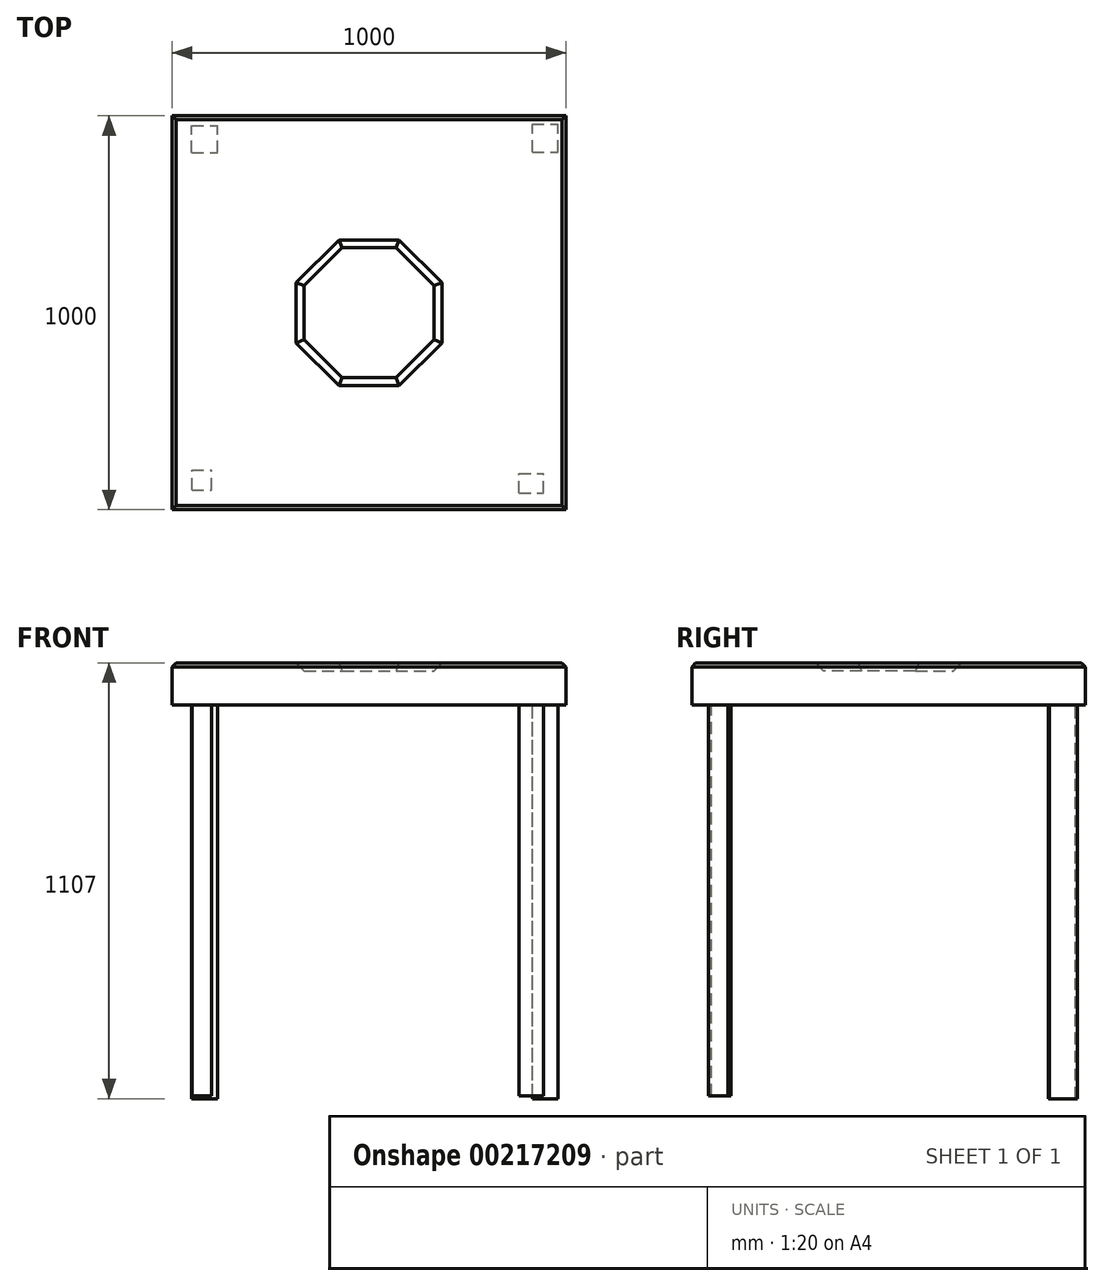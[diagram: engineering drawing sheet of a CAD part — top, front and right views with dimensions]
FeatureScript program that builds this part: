
annotation { "Feature Type Name" : "Feature", "Feature Type Description" : "" }
export const myFeature = defineFeature(function(context is Context, id is Id, definition is map)
    precondition{}
    {
        {
            var Q0;
            Q0=qCreatedBy(makeId("Top.planeOp"),FACE);
            var sketch = newSketch(context, id + "F0", { "sketchPlane" : qUnion([Q0])});
            skLineSegment(sketch, "E0.bottom", {"start": v(500, -500) * mm, "end": v(-500, -500) * mm});
            skLineSegment(sketch, "E0.top", {"start": v(500, 500) * mm, "end": v(-500, 500) * mm});
            skLineSegment(sketch, "E0.left", {"start": v(500, -500) * mm, "end": v(500, 500) * mm});
            skLineSegment(sketch, "E0.right", {"start": v(-500, -500) * mm, "end": v(-500, 500) * mm});
            skPoint(sketch, "E0.middle", {"position": v(0, 0) * mm});
            skSolve(sketch);
        }
        {
            var Q0;
            Q0=makeQuery(id+"F0.imprint","IMPRINT",FACE,{"disambiguationData":[TD([[makeQuery(id+"F0.imprint","IMPRINT",EDGE,{"derivedFrom":sQuery(id+"F0.wireOp",EDGE,"E0.bottom")}),-1.0]])]});
            extrude(context, id + "F1", {"entities" : qUnion([Q0]), "depth" : 100 * mm});
        }
        {
            var Q0;
            Q0=makeQuery(id+"F1.opExtrude","CAP_FACE",FACE,{"disambiguationData":[OSD([sQuery(id+"F0.wireOp",EDGE,"E0.bottom"),sQuery(id+"F0.wireOp",EDGE,"E0.top"),sQuery(id+"F0.wireOp",EDGE,"E0.left"),sQuery(id+"F0.wireOp",EDGE,"E0.right")])],"isStart":false});
            var sketch = newSketch(context, id + "F2", { "sketchPlane" : qUnion([Q0])});
            skCircle(sketch, "E1.cCircle", {"center": v(0, 0) * mm, "radius": 175 * mm, "construction": true});
            skLineSegment(sketch, "E1.0", {"start": v(175, -72.49) * mm, "end": v(72.49, -175) * mm});
            skLineSegment(sketch, "E1.1", {"start": v(72.49, -175) * mm, "end": v(-72.49, -175) * mm});
            skLineSegment(sketch, "E1.2", {"start": v(-72.49, -175) * mm, "end": v(-175, -72.49) * mm});
            skLineSegment(sketch, "E1.3", {"start": v(-175, -72.49) * mm, "end": v(-175, 72.49) * mm});
            skLineSegment(sketch, "E1.4", {"start": v(-175, 72.49) * mm, "end": v(-72.49, 175) * mm});
            skLineSegment(sketch, "E1.5", {"start": v(-72.49, 175) * mm, "end": v(72.49, 175) * mm});
            skLineSegment(sketch, "E1.6", {"start": v(72.49, 175) * mm, "end": v(175, 72.49) * mm});
            skLineSegment(sketch, "E1.7", {"start": v(175, 72.49) * mm, "end": v(175, -72.49) * mm});
            skPoint(sketch, "E1.0.midPoint", {"position": v(123.74, -123.74) * mm});
            skSolve(sketch);
        }
        {
            var Q0;
            Q0=makeQuery(id+"F2.imprint","IMPRINT",FACE,{"disambiguationData":[TD([[makeQuery(id+"F2.imprint","IMPRINT",EDGE,{"derivedFrom":sQuery(id+"F2.wireOp",EDGE,"E1.0")}),-1.0]])]});
            extrude(context, id + "F3", {"entities" : qUnion([Q0]), "operationType" : NewBodyOperationType.REMOVE, "oppositeDirection" : true, "depth" : 20 * mm});
        }
        {
            var Q0;
            Q0=makeQuery(id+"F3.boolean.opBoolean","COPY",FACE,{"derivedFrom":makeQuery(id+"F3.opExtrude","CAP_FACE",FACE,{"disambiguationData":[OSD([sQuery(id+"F2.wireOp",EDGE,"E1.0"),sQuery(id+"F2.wireOp",EDGE,"E1.1"),sQuery(id+"F2.wireOp",EDGE,"E1.2"),sQuery(id+"F2.wireOp",EDGE,"E1.3"),sQuery(id+"F2.wireOp",EDGE,"E1.4"),sQuery(id+"F2.wireOp",EDGE,"E1.5"),sQuery(id+"F2.wireOp",EDGE,"E1.6"),sQuery(id+"F2.wireOp",EDGE,"E1.7")])],"isStart":false})});
            var Q1;
            Q1=makeQuery(id+"F1.opExtrude","CAP_FACE",FACE,{"disambiguationData":[OSD([sQuery(id+"F0.wireOp",EDGE,"E0.bottom"),sQuery(id+"F0.wireOp",EDGE,"E0.top"),sQuery(id+"F0.wireOp",EDGE,"E0.left"),sQuery(id+"F0.wireOp",EDGE,"E0.right")])],"isStart":false});
            chamfer(context, id + "F4", {"entities" : qUnion([Q0, Q1]), "width" : 10 * mm, "tangentPropagation" : true});
        }
        {
            var Q0;
            Q0=makeQuery(id+"F1.opExtrude","CAP_FACE",FACE,{"disambiguationData":[OSD([sQuery(id+"F0.wireOp",EDGE,"E0.bottom"),sQuery(id+"F0.wireOp",EDGE,"E0.top"),sQuery(id+"F0.wireOp",EDGE,"E0.left"),sQuery(id+"F0.wireOp",EDGE,"E0.right")])],"isStart":true});
            var sketch = newSketch(context, id + "F5", { "sketchPlane" : qUnion([Q0])});
            skLineSegment(sketch, "E2.bottom", {"start": v(-450, 450) * mm, "end": v(-400, 450) * mm});
            skLineSegment(sketch, "E2.top", {"start": v(-450, 400) * mm, "end": v(-400, 400) * mm});
            skLineSegment(sketch, "E2.left", {"start": v(-450, 450) * mm, "end": v(-450, 400) * mm});
            skLineSegment(sketch, "E2.right", {"start": v(-400, 450) * mm, "end": v(-400, 400) * mm});
            skSolve(sketch);
        }
        {
            var Q0;
            Q0 = qSketchRegion(id + "F5", true);
            extrude(context, id + "F6", {"entities" : qUnion([Q0]), "operationType" : NewBodyOperationType.ADD, "depth" : 1000 * mm});
        }
        {
            var Q0;
            Q0=makeQuery(id+"F1.opExtrude","CAP_FACE",FACE,{"disambiguationData":[OSD([sQuery(id+"F0.wireOp",EDGE,"E0.bottom"),sQuery(id+"F0.wireOp",EDGE,"E0.top"),sQuery(id+"F0.wireOp",EDGE,"E0.left"),sQuery(id+"F0.wireOp",EDGE,"E0.right")])],"isStart":true});
            var sketch = newSketch(context, id + "F7", { "sketchPlane" : qUnion([Q0])});
            skLineSegment(sketch, "E3.bottom", {"start": v(381.33, 458.2) * mm, "end": v(443, 458.2) * mm});
            skLineSegment(sketch, "E3.top", {"start": v(381.33, 408.2) * mm, "end": v(443, 408.2) * mm});
            skLineSegment(sketch, "E3.left", {"start": v(381.33, 458.2) * mm, "end": v(381.33, 408.2) * mm});
            skLineSegment(sketch, "E3.right", {"start": v(443, 458.2) * mm, "end": v(443, 408.2) * mm});
            skLineSegment(sketch, "E4.bottom", {"start": v(381.33, 408.2) * mm, "end": v(381.33, 408.2) * mm});
            skLineSegment(sketch, "E4.top", {"start": v(381.33, 458.2) * mm, "end": v(381.33, 458.2) * mm});
            skLineSegment(sketch, "E4.left", {"start": v(381.33, 408.2) * mm, "end": v(381.33, 458.2) * mm});
            skLineSegment(sketch, "E4.right", {"start": v(381.33, 408.2) * mm, "end": v(381.33, 458.2) * mm});
            skLineSegment(sketch, "E5.bottom", {"start": v(-457.1, -413.8) * mm, "end": v(-407.1, -413.8) * mm});
            skLineSegment(sketch, "E5.top", {"start": v(-457.1, -463.8) * mm, "end": v(-407.1, -463.8) * mm});
            skLineSegment(sketch, "E5.left", {"start": v(-457.1, -413.8) * mm, "end": v(-457.1, -463.8) * mm});
            skLineSegment(sketch, "E5.right", {"start": v(-407.1, -413.8) * mm, "end": v(-407.1, -463.8) * mm});
            skLineSegment(sketch, "E6.bottom", {"start": v(388.25, -419.8) * mm, "end": v(455.2, -419.8) * mm});
            skLineSegment(sketch, "E6.top", {"start": v(388.25, -463.8) * mm, "end": v(455.2, -463.8) * mm});
            skLineSegment(sketch, "E6.left", {"start": v(388.25, -419.8) * mm, "end": v(388.25, -463.8) * mm});
            skLineSegment(sketch, "E6.right", {"start": v(455.2, -419.8) * mm, "end": v(455.2, -463.8) * mm});
            skLineSegment(sketch, "E7.bottom", {"start": v(388.25, -463.8) * mm, "end": v(388.25, -463.8) * mm});
            skLineSegment(sketch, "E7.top", {"start": v(388.25, -419.8) * mm, "end": v(388.25, -419.8) * mm});
            skLineSegment(sketch, "E7.left", {"start": v(388.25, -463.8) * mm, "end": v(388.25, -419.8) * mm});
            skLineSegment(sketch, "E7.right", {"start": v(388.25, -463.8) * mm, "end": v(388.25, -419.8) * mm});
            skSolve(sketch);
        }
        {
            var Q0;
            Q0=makeQuery(id+"F7.imprint","IMPRINT",FACE,{"disambiguationData":[TD([[makeQuery(id+"F7.imprint","IMPRINT",EDGE,{"derivedFrom":sQuery(id+"F7.wireOp",EDGE,"E3.bottom")}),-1.0]])]});
            extrude(context, id + "F8", {"entities" : qUnion([Q0]), "operationType" : NewBodyOperationType.ADD, "depth" : 1000 * mm});
        }
        {
            var Q0;
            Q0=makeQuery(id+"F1.opExtrude","CAP_FACE",FACE,{"disambiguationData":[OSD([sQuery(id+"F0.wireOp",EDGE,"E0.bottom"),sQuery(id+"F0.wireOp",EDGE,"E0.top"),sQuery(id+"F0.wireOp",EDGE,"E0.left"),sQuery(id+"F0.wireOp",EDGE,"E0.right")])],"isStart":true});
            var sketch = newSketch(context, id + "F9", { "sketchPlane" : qUnion([Q0])});
            skSolve(sketch);
        }
        {
            var Q0;
            Q0=makeQuery(id+"F9.imprint","IMPRINT",FACE,{"disambiguationData":[TD([[makeQuery(id+"F9.imprint","IMPRINT",EDGE,{"derivedFrom":makeQuery(id+"F1.opExtrude","CAP_EDGE",EDGE,{"disambiguationData":[OSD([sQuery(id+"F0.wireOp",EDGE,"E0.bottom")])],"isStart":true})}),1.0]])]});
            var sketch = newSketch(context, id + "F10", { "sketchPlane" : qUnion([Q0])});
            skLineSegment(sketch, "E8.bottom", {"start": v(-437.98, -431.28) * mm, "end": v(-380.6, -431.28) * mm});
            skLineSegment(sketch, "E8.top", {"start": v(-437.98, -488.66) * mm, "end": v(-380.6, -488.66) * mm});
            skLineSegment(sketch, "E8.left", {"start": v(-437.98, -431.28) * mm, "end": v(-437.98, -488.66) * mm});
            skLineSegment(sketch, "E8.right", {"start": v(-380.6, -431.28) * mm, "end": v(-380.6, -488.66) * mm});
            skLineSegment(sketch, "E9.bottom", {"start": v(401.64, -400.68) * mm, "end": v(466.67, -400.68) * mm});
            skLineSegment(sketch, "E9.top", {"start": v(401.64, -477.19) * mm, "end": v(466.67, -477.19) * mm});
            skLineSegment(sketch, "E9.left", {"start": v(401.64, -400.68) * mm, "end": v(401.64, -477.19) * mm});
            skLineSegment(sketch, "E9.right", {"start": v(466.67, -400.68) * mm, "end": v(466.67, -477.19) * mm});
            skSolve(sketch);
        }
        {
            var Q0;
            Q0=makeQuery(id+"F9.imprint","IMPRINT",FACE,{"disambiguationData":[TD([[makeQuery(id+"F9.imprint","IMPRINT",EDGE,{"derivedFrom":makeQuery(id+"F1.opExtrude","CAP_EDGE",EDGE,{"disambiguationData":[OSD([sQuery(id+"F0.wireOp",EDGE,"E0.bottom")])],"isStart":true})}),1.0]])]});
            var Q1;
            Q1 = qSketchRegion(id + "F10", true);
            extrude(context, id + "F11", {"entities" : qUnion([Q0, Q1]), "operationType" : NewBodyOperationType.ADD, "depth" : 7 * mm});
        }
        {
            var Q0;
            Q0=makeQuery(id+"F11.opExtrude","CAP_FACE",FACE,{"disambiguationData":[OSD([sQuery(id+"F0.wireOp",EDGE,"E0.bottom"),sQuery(id+"F0.wireOp",EDGE,"E0.top"),sQuery(id+"F0.wireOp",EDGE,"E0.left"),sQuery(id+"F0.wireOp",EDGE,"E0.right"),sQuery(id+"F5.wireOp",EDGE,"E2.bottom"),sQuery(id+"F5.wireOp",EDGE,"E2.top"),sQuery(id+"F5.wireOp",EDGE,"E2.left"),sQuery(id+"F5.wireOp",EDGE,"E2.right"),sQuery(id+"F7.wireOp",EDGE,"E3.bottom"),sQuery(id+"F7.wireOp",EDGE,"E3.top"),sQuery(id+"F7.wireOp",EDGE,"E3.right"),sQuery(id+"F7.wireOp",EDGE,"E4.right")])],"isStart":false});
            var sketch = newSketch(context, id + "F12", { "sketchPlane" : qUnion([Q0])});
            skLineSegment(sketch, "E10.bottom", {"start": v(-450.4, -406.55) * mm, "end": v(-384.14, -406.55) * mm});
            skLineSegment(sketch, "E10.top", {"start": v(-450.4, -474.88) * mm, "end": v(-384.14, -474.88) * mm});
            skLineSegment(sketch, "E10.left", {"start": v(-450.4, -406.55) * mm, "end": v(-450.4, -474.88) * mm});
            skLineSegment(sketch, "E10.right", {"start": v(-384.14, -406.55) * mm, "end": v(-384.14, -474.88) * mm});
            skSolve(sketch);
        }
        {
            var Q0;
            Q0 = qSketchRegion(id + "F12", true);
            extrude(context, id + "F13", {"entities" : qUnion([Q0]), "operationType" : NewBodyOperationType.ADD, "depth" : 1000 * mm});
        }
        {
            var Q0;
            Q0=makeQuery(id+"F11.opExtrude","CAP_FACE",FACE,{"disambiguationData":[OSD([sQuery(id+"F0.wireOp",EDGE,"E0.bottom"),sQuery(id+"F0.wireOp",EDGE,"E0.top"),sQuery(id+"F0.wireOp",EDGE,"E0.left"),sQuery(id+"F0.wireOp",EDGE,"E0.right"),sQuery(id+"F5.wireOp",EDGE,"E2.bottom"),sQuery(id+"F5.wireOp",EDGE,"E2.top"),sQuery(id+"F5.wireOp",EDGE,"E2.left"),sQuery(id+"F5.wireOp",EDGE,"E2.right"),sQuery(id+"F7.wireOp",EDGE,"E3.bottom"),sQuery(id+"F7.wireOp",EDGE,"E3.top"),sQuery(id+"F7.wireOp",EDGE,"E3.right"),sQuery(id+"F7.wireOp",EDGE,"E4.right")])],"isStart":false});
            var sketch = newSketch(context, id + "F14", { "sketchPlane" : qUnion([Q0])});
            skLineSegment(sketch, "E11.bottom", {"start": v(415.03, -408.33) * mm, "end": v(480.05, -408.33) * mm});
            skLineSegment(sketch, "E11.top", {"start": v(415.03, -479.1) * mm, "end": v(480.05, -479.1) * mm});
            skLineSegment(sketch, "E11.left", {"start": v(415.03, -408.33) * mm, "end": v(415.03, -479.1) * mm});
            skLineSegment(sketch, "E11.right", {"start": v(480.05, -408.33) * mm, "end": v(480.05, -479.1) * mm});
            skSolve(sketch);
        }
        {
            var Q0;
            Q0=makeQuery(id+"F14.imprint","IMPRINT",FACE,{"disambiguationData":[TD([[makeQuery(id+"F14.imprint","IMPRINT",EDGE,{"derivedFrom":sQuery(id+"F14.wireOp",EDGE,"E11.bottom")}),-1.0]])]});
            extrude(context, id + "F15", {"entities" : qUnion([Q0]), "operationType" : NewBodyOperationType.ADD, "depth" : 1000 * mm});
        }
    });
